# Revit family: P4D24
name_source: partatom
category: Lighting Fixtures
revit_build: Autodesk Revit Architecture 2012 (Build: 20110309_2315(x64)
units: mm (PartAtom-declared; Revit-internal decimal feet)

## types (10) — shared parameters
Air Tight = Black
Apparent Load = 0 VA
Color Filter = 16777215
Default Elevation = 48"
Description = High Performance Parabolic
Dimming Lamp Color Temperature Shift = <None>
Emit from Line Length = 24"
Finish = Steel
Glass = Glass
Lamp = Two,Three,Four
Manufacturer = Columbia Lighting
Manufacturer Fax = (864)-678-1065
Model = P4D24
Product Page URL = http://www.columbialighting.com
Product Specification Sheet = http://www.columbialighting.com
Tilt Angle = 90.00°
URL = http://www.columbialighting.com
Wattage Comments = 56 W

## per-type parameters (varying)
| type | Photometric Web File |
| P4D24-232-LD26-E | 12449 |
| P4D24-232-MA26 | 12454 |
| P4D24-232-MA28 | 12501 |
| P4D24-232-MA46 | 12502 |
| P4D24-232-MA48 | 12468 |
| P4D24-332G-LD36-E | 12446 |
| P4D24-332-MA36 | 12453 |
| P4D24-432-MA28 | 12500 |
| P4D24-432-MA46 | 12499 |
| P4D24-432-MA48 | 12452 |

## geometry (parser evidence)
native form markers: Blend x2, Sweep x1
no freeform markers — native parametric forms only
